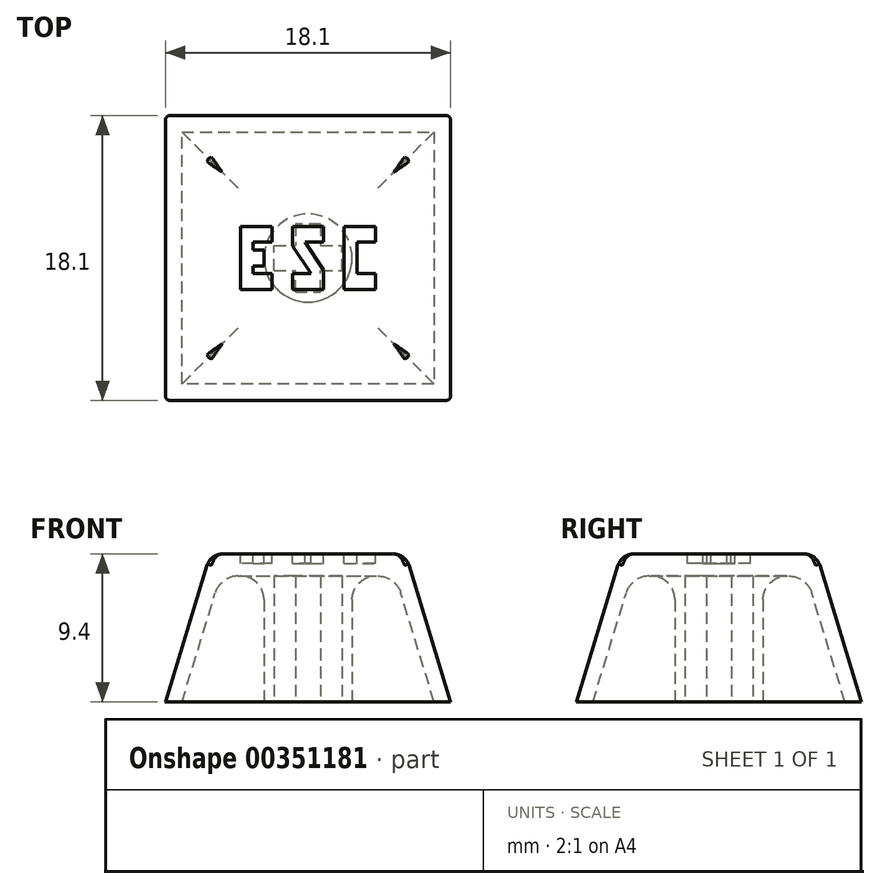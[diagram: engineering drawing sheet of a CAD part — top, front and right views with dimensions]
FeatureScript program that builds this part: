
annotation { "Feature Type Name" : "Feature", "Feature Type Description" : "" }
export const myFeature = defineFeature(function(context is Context, id is Id, definition is map)
    precondition{}
    {
        {
            var Q0;
            Q0=qCreatedBy(makeId("Front.planeOp"),FACE);
            var sketch = newSketch(context, id + "F0", { "sketchPlane" : qUnion([Q0])});
            skLineSegment(sketch, "E0", {"start": v(-8, 0) * mm, "end": v(-5.57, 8) * mm});
            skLineSegment(sketch, "E1", {"start": v(-5.57, 8) * mm, "end": v(5.57, 8) * mm});
            skLineSegment(sketch, "E2", {"start": v(5.57, 8) * mm, "end": v(8, 0) * mm});
            skLineSegment(sketch, "E3", {"start": v(8, 0) * mm, "end": v(9.05, 0) * mm});
            skLineSegment(sketch, "E4", {"start": v(9.05, 0) * mm, "end": v(6.18, 9.4) * mm});
            skLineSegment(sketch, "E5", {"start": v(-6.19, 9.4) * mm, "end": v(-9.05, 0) * mm});
            skLineSegment(sketch, "E6", {"start": v(-9.05, 0) * mm, "end": v(-8, 0) * mm});
            skLineSegment(sketch, "E7", {"start": v(6.18, 9.4) * mm, "end": v(-6.18, 9.4) * mm});
            skSolve(sketch);
        }
        {
            var Q0;
            Q0=qCreatedBy(makeId("Top.planeOp"),FACE);
            var sketch = newSketch(context, id + "F1", { "sketchPlane" : qUnion([Q0])});
            skLineSegment(sketch, "E8.0", {"start": v(-9.05, 0) * mm, "end": v(-8, 0) * mm});
            skLineSegment(sketch, "E9.0", {"start": v(8, 0) * mm, "end": v(9.05, 0) * mm});
            skLineSegment(sketch, "E10.bottom", {"start": v(-8.53, 8.53) * mm, "end": v(8.53, 8.53) * mm});
            skLineSegment(sketch, "E10.top", {"start": v(-8.53, -8.53) * mm, "end": v(8.53, -8.53) * mm});
            skLineSegment(sketch, "E10.left", {"start": v(-8.53, 8.53) * mm, "end": v(-8.53, -8.53) * mm});
            skLineSegment(sketch, "E10.right", {"start": v(8.53, 8.53) * mm, "end": v(8.53, -8.53) * mm});
            skPoint(sketch, "E10.middle", {"position": v(0, 0) * mm});
            skSolve(sketch);
        }
        {
            var Q0;
            Q0=makeQuery(id+"F0.imprint","IMPRINT",FACE,{"disambiguationData":[TD([[makeQuery(id+"F0.imprint","IMPRINT",EDGE,{"derivedFrom":sQuery(id+"F0.wireOp",EDGE,"E0")}),1.0]])]});
            var Q1;
            Q1=sQuery(id+"F1.wireOp",EDGE,"E10.left");
            var Q2;
            Q2=sQuery(id+"F1.wireOp",EDGE,"E10.bottom");
            var Q3;
            Q3=sQuery(id+"F1.wireOp",EDGE,"E10.right");
            var Q4;
            Q4=sQuery(id+"F1.wireOp",EDGE,"E10.top");
            sweep(context, id + "F2", {"profiles" : qUnion([Q0]), "path" : qUnion([Q1, Q2, Q3, Q4])});
        }
        {
            var Q0;
            Q0=qCreatedBy(makeId("Top.planeOp"),FACE);
            var sketch = newSketch(context, id + "F3", { "sketchPlane" : qUnion([Q0])});
            skCircle(sketch, "E11", {"center": v(0, 0) * mm, "radius": 2.8 * mm});
            skLineSegment(sketch, "E12.bottom", {"start": v(-2.15, -0.8) * mm, "end": v(-0.8, -0.8) * mm});
            skLineSegment(sketch, "E12.top", {"start": v(-2.15, 0.8) * mm, "end": v(-0.8, 0.8) * mm});
            skLineSegment(sketch, "E12.left", {"start": v(-2.15, -0.8) * mm, "end": v(-2.15, 0.8) * mm});
            skLineSegment(sketch, "E12.right", {"start": v(2.15, -0.8) * mm, "end": v(2.15, 0.8) * mm});
            skLineSegment(sketch, "E13.bottom", {"start": v(-0.8, -2.15) * mm, "end": v(0.8, -2.15) * mm});
            skLineSegment(sketch, "E13.top", {"start": v(-0.8, 2.15) * mm, "end": v(0.8, 2.15) * mm});
            skLineSegment(sketch, "E13.right", {"start": v(0.8, -2.15) * mm, "end": v(0.8, -0.8) * mm});
            skLineSegment(sketch, "E14.trimOffspring", {"start": v(0.8, 0.8) * mm, "end": v(0.8, 2.15) * mm});
            skLineSegment(sketch, "E15.trimOffspring", {"start": v(0.8, -0.8) * mm, "end": v(2.15, -0.8) * mm});
            skLineSegment(sketch, "E16.trimOffspring", {"start": v(-0.8, 0.8) * mm, "end": v(-0.8, 2.15) * mm});
            skLineSegment(sketch, "E17.trimOffspring", {"start": v(0.8, 0.8) * mm, "end": v(2.15, 0.8) * mm});
            skLineSegment(sketch, "E18", {"start": v(-0.8, -2.15) * mm, "end": v(-0.8, -0.8) * mm});
            skSolve(sketch);
        }
        {
            var Q0;
            Q0=makeQuery(id+"F3.imprint","IMPRINT",FACE,{"disambiguationData":[TD([[makeQuery(id+"F3.imprint","IMPRINT",EDGE,{"derivedFrom":sQuery(id+"F3.wireOp",EDGE,"E11")}),1.0]])]});
            var Q1;
            Q1=makeQuery(id+"F2.opSweep","SWEPT_FACE",FACE,{"disambiguationData":[OSD([sQuery(id+"F0.wireOp",EDGE,"E1"),sQuery(id+"F1.wireOp",EDGE,"E10.left")])]});
            extrude(context, id + "F4", {"entities" : qUnion([Q0]), "operationType" : NewBodyOperationType.ADD, "endBound" : BoundingType.UP_TO_SURFACE, "endBoundEntityFace" : qUnion([Q1]), "depth" : 25 * mm});
        }
        {
            var Q0;
            Q0=makeQuery(id+"F2.opSweep","SWEPT_EDGE",EDGE,{"disambiguationData":[OSD([sQuery(id+"F0.wireOp",EDGE,"E4"),sQuery(id+"F0.wireOp",EDGE,"E7"),sQuery(id+"F1.wireOp",EDGE,"E10.top")])]});
            var Q1;
            Q1=makeQuery(id+"F2.opSweep","SWEPT_EDGE",EDGE,{"disambiguationData":[OSD([sQuery(id+"F0.wireOp",EDGE,"E4"),sQuery(id+"F0.wireOp",EDGE,"E7"),sQuery(id+"F1.wireOp",EDGE,"E10.right")])]});
            var Q2;
            Q2=makeQuery(id+"F2.opSweep","SWEPT_EDGE",EDGE,{"disambiguationData":[OSD([sQuery(id+"F0.wireOp",EDGE,"E4"),sQuery(id+"F0.wireOp",EDGE,"E7"),sQuery(id+"F1.wireOp",EDGE,"E10.bottom")])]});
            var Q3;
            Q3=makeQuery(id+"F2.opSweep","SWEPT_EDGE",EDGE,{"disambiguationData":[OSD([sQuery(id+"F0.wireOp",EDGE,"E4"),sQuery(id+"F0.wireOp",EDGE,"E7"),sQuery(id+"F1.wireOp",EDGE,"E10.left")])]});
            fillet(context, id + "F5", {"entities" : qUnion([Q0, Q1, Q2, Q3]), "radius" : 1 * mm, "tangentPropagation" : true, "allowEdgeOverflow" : false});
        }
        {
            var Q0;
            Q0=makeQuery(id+"F2.opSweep","MID_CAP_EDGE",EDGE,{"disambiguationData":[OSD([sQuery(id+"F0.wireOp",EDGE,"E4"),sQuery(id+"F1.wireOp",VERTEX,"E10.top.start")])],"capPos":2.0});
            var Q1;
            Q1=makeQuery(id+"F2.opSweep","MID_CAP_EDGE",EDGE,{"disambiguationData":[OSD([sQuery(id+"F0.wireOp",EDGE,"E4"),sQuery(id+"F1.wireOp",VERTEX,"E10.top.end")])],"capPos":1.0});
            var Q2;
            Q2=makeQuery(id+"F2.opSweep","CAP_EDGE",EDGE,{"disambiguationData":[OSD([sQuery(id+"F0.wireOp",EDGE,"E4"),sQuery(id+"F1.wireOp",VERTEX,"E10.right.start")])],"isStart":true});
            var Q3;
            Q3=makeQuery(id+"F2.opSweep","MID_CAP_EDGE",EDGE,{"disambiguationData":[OSD([sQuery(id+"F0.wireOp",EDGE,"E4"),sQuery(id+"F1.wireOp",VERTEX,"E10.bottom.start")])],"capPos":3.0});
            fillet(context, id + "F6", {"entities" : qUnion([Q0, Q1, Q2, Q3]), "radius" : 0.3 * mm, "tangentPropagation" : true, "allowEdgeOverflow" : false});
        }
        {
            var Q0;
            Q0=makeQuery(id+"F4.opExtrude","CAP_EDGE",EDGE,{"disambiguationData":[OSD([sQuery(id+"F3.wireOp",EDGE,"E11")])],"isStart":false});
            var Q1;
            Q1=makeQuery(id+"F2.opSweep","SWEPT_EDGE",EDGE,{"disambiguationData":[OSD([sQuery(id+"F0.wireOp",EDGE,"E1"),sQuery(id+"F0.wireOp",EDGE,"E2"),sQuery(id+"F1.wireOp",EDGE,"E10.right")])]});
            var Q2;
            Q2=makeQuery(id+"F2.opSweep","SWEPT_EDGE",EDGE,{"disambiguationData":[OSD([sQuery(id+"F0.wireOp",EDGE,"E1"),sQuery(id+"F0.wireOp",EDGE,"E2"),sQuery(id+"F1.wireOp",EDGE,"E10.top")])]});
            var Q3;
            Q3=makeQuery(id+"F2.opSweep","SWEPT_EDGE",EDGE,{"disambiguationData":[OSD([sQuery(id+"F0.wireOp",EDGE,"E1"),sQuery(id+"F0.wireOp",EDGE,"E2"),sQuery(id+"F1.wireOp",EDGE,"E10.left")])]});
            var Q4;
            Q4=makeQuery(id+"F2.opSweep","SWEPT_EDGE",EDGE,{"disambiguationData":[OSD([sQuery(id+"F0.wireOp",EDGE,"E1"),sQuery(id+"F0.wireOp",EDGE,"E2"),sQuery(id+"F1.wireOp",EDGE,"E10.bottom")])]});
            fillet(context, id + "F7", {"entities" : qUnion([Q0, Q1, Q2, Q3, Q4]), "radius" : 1.5 * mm, "tangentPropagation" : true, "allowEdgeOverflow" : false});
        }
        {
            var Q0;
            Q0=makeQuery(id+"F2.opSweep","SWEPT_FACE",FACE,{"disambiguationData":[OSD([sQuery(id+"F0.wireOp",EDGE,"E7"),sQuery(id+"F1.wireOp",EDGE,"E10.right")])]});
            var sketch = newSketch(context, id + "F8", { "sketchPlane" : qUnion([Q0])});
            skLineSegment(sketch, "E19.0.0", {"start": v(-5.44, -5.44) * mm, "end": v(5.44, -5.44) * mm});
            skLineSegment(sketch, "E19.0.1", {"start": v(5.44, -5.44) * mm, "end": v(5.44, 5.44) * mm});
            skLineSegment(sketch, "E19.0.2", {"start": v(5.44, 5.44) * mm, "end": v(-5.44, 5.44) * mm});
            skLineSegment(sketch, "E19.0.3", {"start": v(-5.44, 5.44) * mm, "end": v(-5.44, -5.44) * mm});
            skLineSegment(sketch, "E20", {"start": v(-4.3, 2) * mm, "end": v(-4.3, -2) * mm});
            skLineSegment(sketch, "E21", {"start": v(-4.3, -2) * mm, "end": v(-2.3, -2) * mm});
            skLineSegment(sketch, "E22", {"start": v(-2.3, -2) * mm, "end": v(-2.3, -1) * mm});
            skLineSegment(sketch, "E23", {"start": v(-2.3, -1) * mm, "end": v(-3.5, -1) * mm});
            skLineSegment(sketch, "E24", {"start": v(-3.5, -1) * mm, "end": v(-3.5, -0.5) * mm});
            skLineSegment(sketch, "E25", {"start": v(-3.5, -0.5) * mm, "end": v(-2.8, -0.5) * mm});
            skLineSegment(sketch, "E26", {"start": v(-2.8, -0.5) * mm, "end": v(-2.8, 0.5) * mm});
            skLineSegment(sketch, "E27", {"start": v(-2.8, 0.5) * mm, "end": v(-3.5, 0.5) * mm});
            skLineSegment(sketch, "E28", {"start": v(-3.5, 0.5) * mm, "end": v(-3.5, 1) * mm});
            skLineSegment(sketch, "E29", {"start": v(-3.5, 1) * mm, "end": v(-2.3, 1) * mm});
            skLineSegment(sketch, "E30", {"start": v(-2.3, 1) * mm, "end": v(-2.3, 2) * mm});
            skLineSegment(sketch, "E31", {"start": v(-2.3, 2) * mm, "end": v(-4.3, 2) * mm});
            skLineSegment(sketch, "E32.bottom", {"start": v(-1, 2) * mm, "end": v(1, 2) * mm});
            skLineSegment(sketch, "E32.top", {"start": v(-1, -2) * mm, "end": v(1, -2) * mm});
            skLineSegment(sketch, "E32.left", {"start": v(-1, 2) * mm, "end": v(-1, 0.75) * mm});
            skLineSegment(sketch, "E32.right", {"start": v(1, 2) * mm, "end": v(1, 1) * mm});
            skLineSegment(sketch, "E33", {"start": v(-1, -1) * mm, "end": v(0.2, -1) * mm});
            skLineSegment(sketch, "E34", {"start": v(0.2, -1) * mm, "end": v(-1, 0.75) * mm});
            skLineSegment(sketch, "E35", {"start": v(1, 1) * mm, "end": v(-0.2, 1) * mm});
            skLineSegment(sketch, "E36", {"start": v(-0.2, 1) * mm, "end": v(1, -0.75) * mm});
            skLineSegment(sketch, "E37.bottom", {"start": v(2.3, 2) * mm, "end": v(4.3, 2) * mm});
            skLineSegment(sketch, "E37.top", {"start": v(2.3, -2) * mm, "end": v(4.3, -2) * mm});
            skLineSegment(sketch, "E37.left", {"start": v(2.3, 2) * mm, "end": v(2.3, -2) * mm});
            skLineSegment(sketch, "E37.right", {"start": v(4.3, 2) * mm, "end": v(4.3, 1) * mm});
            skLineSegment(sketch, "E38.bottom", {"start": v(4.3, 1) * mm, "end": v(3.1, 1) * mm});
            skLineSegment(sketch, "E38.top", {"start": v(4.3, -1) * mm, "end": v(3.1, -1) * mm});
            skLineSegment(sketch, "E38.right", {"start": v(3.1, 1) * mm, "end": v(3.1, -1) * mm});
            skLineSegment(sketch, "E39.trimOffspring", {"start": v(1, -0.75) * mm, "end": v(1, -2) * mm});
            skLineSegment(sketch, "E40.trimOffspring", {"start": v(-1, -1) * mm, "end": v(-1, -2) * mm});
            skLineSegment(sketch, "E41.trimOffspring", {"start": v(4.3, -1) * mm, "end": v(4.3, -2) * mm});
            skSolve(sketch);
        }
        {
            var Q0;
            Q0=makeQuery(id+"F8.imprint","IMPRINT",FACE,{"disambiguationData":[TD([[makeQuery(id+"F8.imprint","IMPRINT",EDGE,{"derivedFrom":sQuery(id+"F8.wireOp",EDGE,"E20")}),1.0]])]});
            var Q1;
            Q1=makeQuery(id+"F8.imprint","IMPRINT",FACE,{"disambiguationData":[TD([[makeQuery(id+"F8.imprint","IMPRINT",EDGE,{"derivedFrom":sQuery(id+"F8.wireOp",EDGE,"E32.bottom")}),-1.0]])]});
            var Q2;
            Q2=makeQuery(id+"F8.imprint","IMPRINT",FACE,{"disambiguationData":[TD([[makeQuery(id+"F8.imprint","IMPRINT",EDGE,{"derivedFrom":sQuery(id+"F8.wireOp",EDGE,"E37.bottom")}),-1.0]])]});
            extrude(context, id + "F9", {"entities" : qUnion([Q0, Q1, Q2]), "operationType" : NewBodyOperationType.REMOVE, "oppositeDirection" : true, "depth" : 0.6 * mm});
        }
    });
